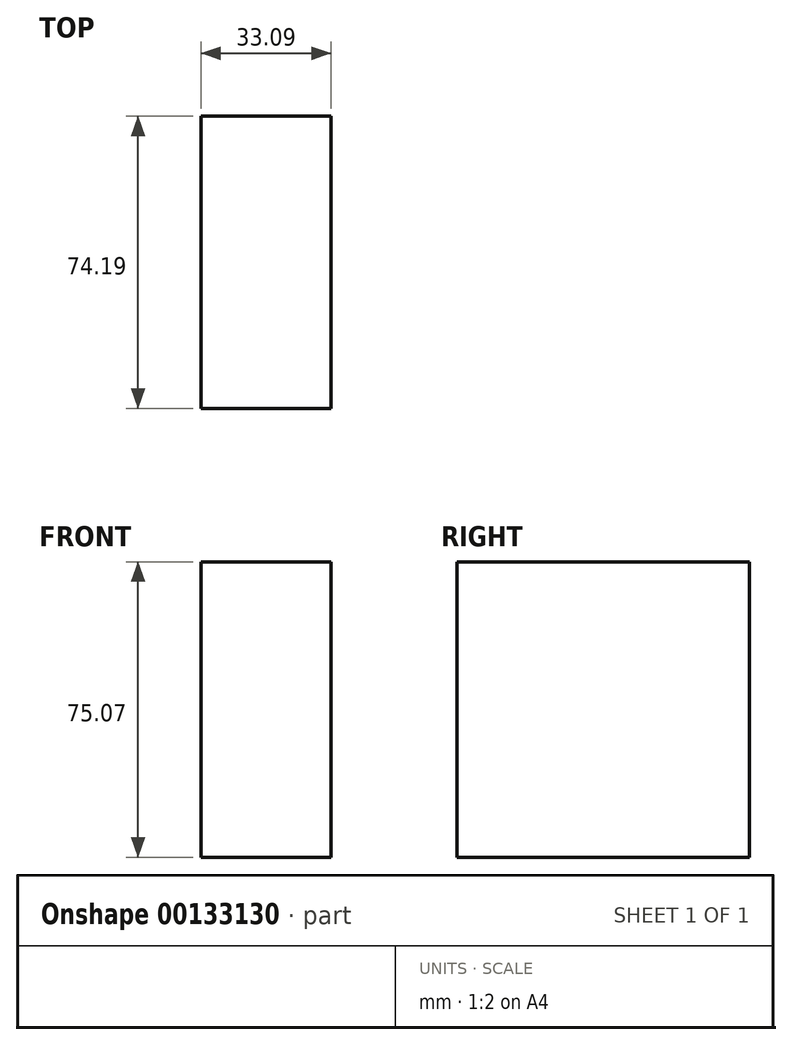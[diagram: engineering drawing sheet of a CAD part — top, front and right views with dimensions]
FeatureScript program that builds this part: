
annotation { "Feature Type Name" : "Feature", "Feature Type Description" : "" }
export const myFeature = defineFeature(function(context is Context, id is Id, definition is map)
    precondition{}
    {
        {
            var Q0;
            Q0=qCreatedBy(makeId("Front.planeOp"),FACE);
            var sketch = newSketch(context, id + "F0", { "sketchPlane" : qUnion([Q0])});
            skLineSegment(sketch, "E0.bottom", {"start": v(15.27, 41.94) * mm, "end": v(-17.82, 41.94) * mm});
            skLineSegment(sketch, "E0.top", {"start": v(15.27, -33.13) * mm, "end": v(-17.82, -33.13) * mm});
            skLineSegment(sketch, "E0.left", {"start": v(15.27, 41.94) * mm, "end": v(15.27, -33.13) * mm});
            skLineSegment(sketch, "E0.right", {"start": v(-17.82, 41.94) * mm, "end": v(-17.82, -33.13) * mm});
            skSolve(sketch);
        }
        {
            var Q0;
            Q0=makeQuery(id+"F0.imprint","IMPRINT",FACE,{"disambiguationData":[TD([[makeQuery(id+"F0.imprint","IMPRINT",EDGE,{"derivedFrom":sQuery(id+"F0.wireOp",EDGE,"E0.bottom")}),1.0]])]});
            extrude(context, id + "F1", {"entities" : qUnion([Q0]), "depth" : 74.19 * mm});
        }
    });
